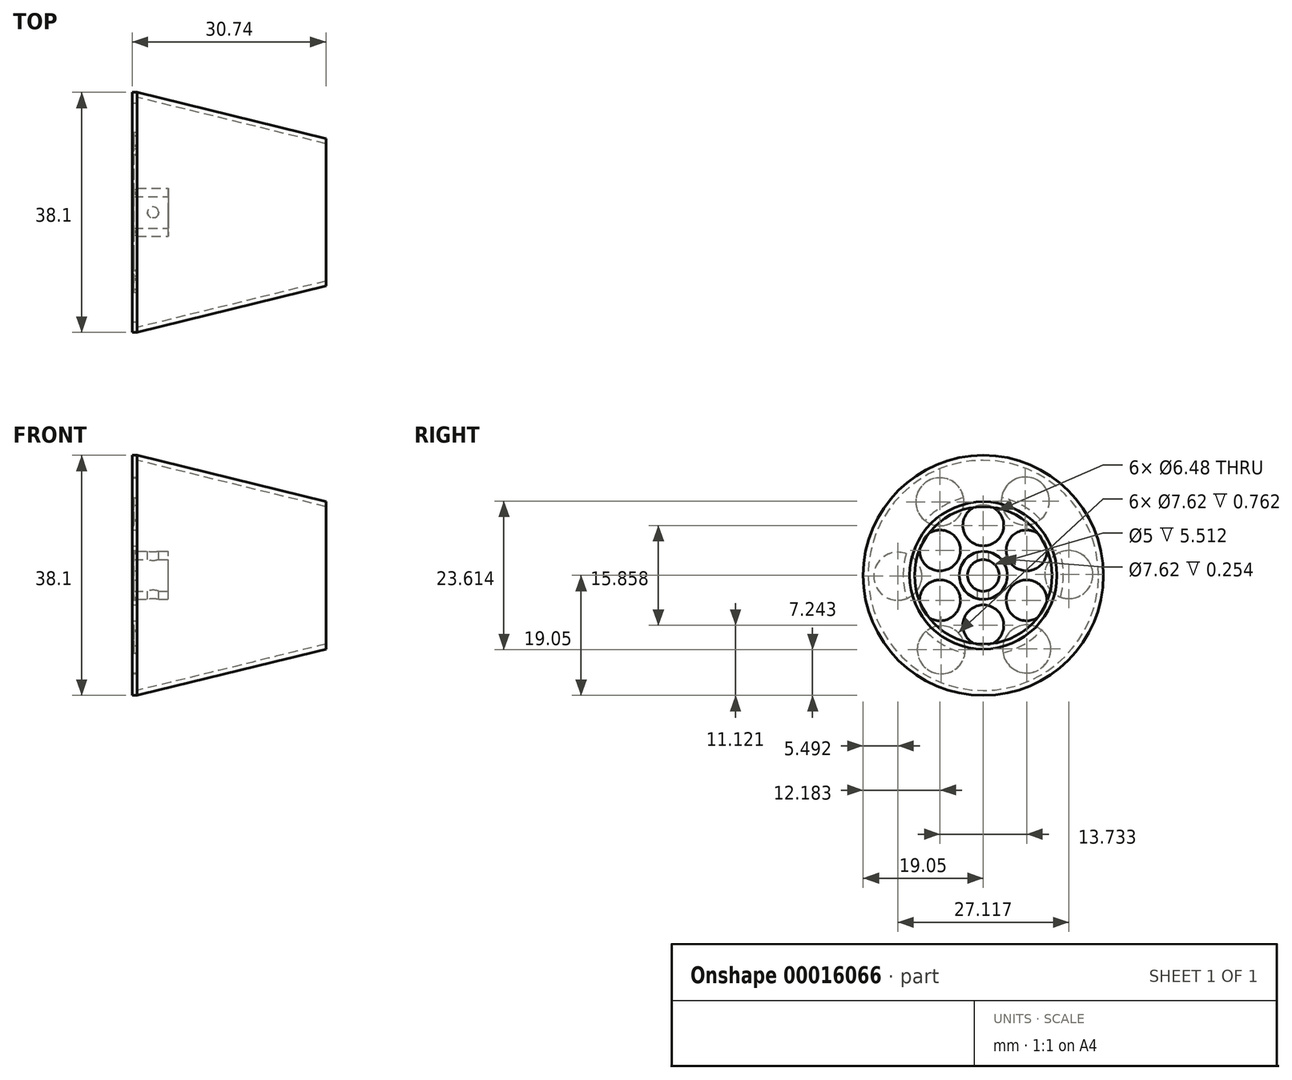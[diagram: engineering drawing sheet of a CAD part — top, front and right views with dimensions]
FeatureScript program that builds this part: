
annotation { "Feature Type Name" : "Feature", "Feature Type Description" : "" }
export const myFeature = defineFeature(function(context is Context, id is Id, definition is map)
    precondition{}
    {
        {
            var Q0;
            Q0=qCreatedBy(makeId("Right.planeOp"),FACE);
            var sketch = newSketch(context, id + "F0", { "sketchPlane" : qUnion([Q0])});
            skCircle(sketch, "E0", {"center": v(0, 0) * mm, "radius": 2.5 * mm});
            skCircle(sketch, "E1", {"center": v(0, 0) * mm, "radius": 3.81 * mm});
            skSolve(sketch);
        }
        {
            var Q0;
            Q0=makeQuery(id+"F0.imprint","IMPRINT",FACE,{"disambiguationData":[TD([[makeQuery(id+"F0.imprint","IMPRINT",EDGE,{"derivedFrom":sQuery(id+"F0.wireOp",EDGE,"E0")}),-1.0]])]});
            extrude(context, id + "F1", {"entities" : qUnion([Q0]), "oppositeDirection" : true, "depth" : 5 * mm});
        }
        {
            var Q0;
            Q0=qCreatedBy(makeId("Top.planeOp"),FACE);
            var sketch = newSketch(context, id + "F2", { "sketchPlane" : qUnion([Q0])});
            skCircle(sketch, "E2", {"center": v(-2.45, 0) * mm, "radius": 0.89 * mm});
            skSolve(sketch);
        }
        {
            var Q0;
            Q0=makeQuery(id+"F2.imprint","IMPRINT",FACE,{"disambiguationData":[TD([[makeQuery(id+"F2.imprint","IMPRINT",EDGE,{"derivedFrom":sQuery(id+"F2.wireOp",EDGE,"E2")}),1.0]])]});
            extrude(context, id + "F3", {"entities" : qUnion([Q0]), "operationType" : NewBodyOperationType.REMOVE, "endBound" : BoundingType.SYMMETRIC, "oppositeDirection" : true, "depth" : 25.4 * mm});
        }
        {
            var Q0;
            Q0=makeQuery(id+"F1.opExtrude","CAP_FACE",FACE,{"disambiguationData":[OSD([sQuery(id+"F0.wireOp",EDGE,"E0"),sQuery(id+"F0.wireOp",EDGE,"E1")])],"isStart":false});
            var sketch = newSketch(context, id + "F4", { "sketchPlane" : qUnion([Q0])});
            skCircle(sketch, "E3", {"center": v(0, 0) * mm, "radius": 12.7 * mm});
            skCircle(sketch, "E4", {"center": v(0, 7.93) * mm, "radius": 3.24 * mm});
            skCircle(sketch, "E5.1.0", {"center": v(-6.87, 3.96) * mm, "radius": 3.24 * mm});
            skCircle(sketch, "E5.2.0", {"center": v(-6.87, -3.96) * mm, "radius": 3.24 * mm});
            skCircle(sketch, "E5.3.0", {"center": v(0, -7.93) * mm, "radius": 3.24 * mm});
            skCircle(sketch, "E5.4.0", {"center": v(6.87, -3.96) * mm, "radius": 3.24 * mm});
            skCircle(sketch, "E5.5.0", {"center": v(6.87, 3.96) * mm, "radius": 3.24 * mm});
            skSolve(sketch);
        }
        {
            var Q0;
            Q0=makeQuery(id+"F4.imprint","IMPRINT",FACE,{"disambiguationData":[TD([[makeQuery(id+"F4.imprint","IMPRINT",EDGE,{"derivedFrom":makeQuery(id+"F1.opExtrude","CAP_EDGE",EDGE,{"disambiguationData":[OSD([sQuery(id+"F0.wireOp",EDGE,"E0")])],"isStart":false})}),1.0]])]});
            var Q1;
            Q1=makeQuery(id+"F4.imprint","IMPRINT",FACE,{"disambiguationData":[TD([[makeQuery(id+"F4.imprint","IMPRINT",EDGE,{"derivedFrom":sQuery(id+"F4.wireOp",EDGE,"E3")}),1.0]])]});
            extrude(context, id + "F5", {"entities" : qUnion([Q0, Q1]), "operationType" : NewBodyOperationType.ADD, "depth" : 0.5 * mm});
        }
        {
            var Q0;
            Q0=makeQuery(id+"F5.opExtrude","CAP_FACE",FACE,{"disambiguationData":[OSD([sQuery(id+"F0.wireOp",EDGE,"E0"),sQuery(id+"F4.wireOp",EDGE,"E3"),sQuery(id+"F4.wireOp",EDGE,"E4"),sQuery(id+"F4.wireOp",EDGE,"E5.1.0"),sQuery(id+"F4.wireOp",EDGE,"E5.2.0"),sQuery(id+"F4.wireOp",EDGE,"E5.3.0"),sQuery(id+"F4.wireOp",EDGE,"E5.4.0"),sQuery(id+"F4.wireOp",EDGE,"E5.5.0")])],"isStart":true});
            var sketch = newSketch(context, id + "F6", { "sketchPlane" : qUnion([Q0])});
            skCircle(sketch, "E6", {"center": v(0, 0) * mm, "radius": 12.7 * mm});
            skSolve(sketch);
        }
        {
            var Q0;
            Q0 = qSketchRegion(id + "F6", true);
            extrude(context, id + "F7", {"entities" : qUnion([Q0]), "depth" : 30 * mm, "hasDraft" : true, "draftAngle" : 2.5 * degree, "draftPullDirection" : true});
        }
        {
            var Q0;
            Q0=makeQuery(id+"F7.opExtrude","CAP_FACE",FACE,{"disambiguationData":[OSD([sQuery(id+"F6.wireOp",EDGE,"E6")])],"isStart":false});
            var Q1;
            Q1=makeQuery(id+"F7.opExtrude","CAP_FACE",FACE,{"disambiguationData":[OSD([sQuery(id+"F6.wireOp",EDGE,"E6")])],"isStart":true});
            var Q2;
            Q2=makeQuery(id+"F7.opExtrude","SWEPT_BODY",BODY,{"disambiguationData":[OSD([sQuery(id+"F6.wireOp",EDGE,"E6")])]});
            shell(context, id + "F8", {"entities" : qUnion([Q0, Q1]), "parts" : qUnion([Q2]), "thickness" : 0.76 * mm});
        }
        {
            var Q0;
            Q0=makeQuery(id+"F7.opExtrude","CAP_FACE",FACE,{"disambiguationData":[OSD([sQuery(id+"F6.wireOp",EDGE,"E6")])],"isStart":false});
            var sketch = newSketch(context, id + "F9", { "sketchPlane" : qUnion([Q0])});
            skCircle(sketch, "E7.0", {"center": v(0, 0) * mm, "radius": 11.4 * mm});
            skCircle(sketch, "E8", {"center": v(0, 0) * mm, "radius": 11.35 * mm});
            skSolve(sketch);
        }
        {
            var Q0;
            Q0=makeQuery(id+"F7.opExtrude","SWEPT_BODY",BODY,{"disambiguationData":[OSD([sQuery(id+"F6.wireOp",EDGE,"E6")])]});
            deleteBodies(context, id + "F10", {"entities" : qUnion([Q0])});
        }
        {
            var Q0;
            Q0=makeQuery(id+"F5.opExtrude","CAP_FACE",FACE,{"disambiguationData":[OSD([sQuery(id+"F0.wireOp",EDGE,"E0"),sQuery(id+"F4.wireOp",EDGE,"E3"),sQuery(id+"F4.wireOp",EDGE,"E4"),sQuery(id+"F4.wireOp",EDGE,"E5.1.0"),sQuery(id+"F4.wireOp",EDGE,"E5.2.0"),sQuery(id+"F4.wireOp",EDGE,"E5.3.0"),sQuery(id+"F4.wireOp",EDGE,"E5.4.0"),sQuery(id+"F4.wireOp",EDGE,"E5.5.0")])],"isStart":true});
            var sketch = newSketch(context, id + "F11", { "sketchPlane" : qUnion([Q0])});
            skCircle(sketch, "E9", {"center": v(0, 0) * mm, "radius": 19.05 * mm});
            skCircle(sketch, "E10", {"center": v(-6.9, 11.68) * mm, "radius": 3.81 * mm});
            skCircle(sketch, "E11.1.0", {"center": v(-13.56, -0.13) * mm, "radius": 3.81 * mm});
            skCircle(sketch, "E11.2.0", {"center": v(-6.67, -11.8) * mm, "radius": 3.81 * mm});
            skCircle(sketch, "E11.3.0", {"center": v(6.9, -11.68) * mm, "radius": 3.81 * mm});
            skCircle(sketch, "E11.4.0", {"center": v(13.56, 0.13) * mm, "radius": 3.81 * mm});
            skCircle(sketch, "E11.5.0", {"center": v(6.67, 11.8) * mm, "radius": 3.81 * mm});
            skSolve(sketch);
        }
        {
            var Q0;
            Q0=makeQuery(id+"F11.imprint","IMPRINT",FACE,{"disambiguationData":[TD([[makeQuery(id+"F11.imprint","IMPRINT",EDGE,{"derivedFrom":sQuery(id+"F11.wireOp",EDGE,"E9")}),1.0]])]});
            var Q1;
            Q1=makeQuery(id+"F11.imprint","IMPRINT",FACE,{"disambiguationData":[TD([[makeQuery(id+"F11.imprint","IMPRINT",EDGE,{"derivedFrom":makeQuery(id+"F5.opExtrude","CAP_EDGE",EDGE,{"disambiguationData":[OSD([sQuery(id+"F4.wireOp",EDGE,"E4")])],"isStart":true})}),1.0]])]});
            extrude(context, id + "F12", {"entities" : qUnion([Q0, Q1]), "operationType" : NewBodyOperationType.ADD, "oppositeDirection" : true, "depth" : 0.76 * mm});
        }
        {
            var Q0;
            {var subQ0=sQuery(id+"F4.wireOp",EDGE,"E4");var subQ1=sQuery(id+"F4.wireOp",EDGE,"E5.1.0");var subQ2=sQuery(id+"F4.wireOp",EDGE,"E5.2.0");var subQ3=sQuery(id+"F4.wireOp",EDGE,"E5.3.0");var subQ4=sQuery(id+"F4.wireOp",EDGE,"E5.4.0");var subQ5=sQuery(id+"F4.wireOp",EDGE,"E5.5.0");Q0=makeQuery(id+"F12.boolean.opBoolean","MERGE",FACE,{"derivedFrom":[makeQuery(id+"F5.opExtrude","CAP_FACE",FACE,{"disambiguationData":[OSD([sQuery(id+"F0.wireOp",EDGE,"E0"),sQuery(id+"F4.wireOp",EDGE,"E3"),subQ0,subQ1,subQ2,subQ3,subQ4,subQ5])],"isStart":true}),makeQuery(id+"F12.opExtrude","CAP_FACE",FACE,{"disambiguationData":[OSD([sQuery(id+"F0.wireOp",EDGE,"E1"),subQ0,subQ1,subQ2,subQ3,subQ4,subQ5,sQuery(id+"F11.wireOp",EDGE,"E9"),sQuery(id+"F11.wireOp",EDGE,"E10"),sQuery(id+"F11.wireOp",EDGE,"E11.1.0"),sQuery(id+"F11.wireOp",EDGE,"E11.2.0"),sQuery(id+"F11.wireOp",EDGE,"E11.3.0"),sQuery(id+"F11.wireOp",EDGE,"E11.4.0"),sQuery(id+"F11.wireOp",EDGE,"E11.5.0")])],"isStart":true})]});}
            var sketch = newSketch(context, id + "F13", { "sketchPlane" : qUnion([Q0])});
            skCircle(sketch, "E12", {"center": v(0, 0) * mm, "radius": 19.05 * mm});
            skSolve(sketch);
        }
        {
            var Q0;
            Q0 = qSketchRegion(id + "F13", true);
            extrude(context, id + "F14", {"entities" : qUnion([Q0]), "depth" : 29.97 * mm, "hasDraft" : true, "draftAngle" : 13.8 * degree, "draftPullDirection" : true});
        }
        {
            var Q0;
            Q0=makeQuery(id+"F14.opExtrude","CAP_FACE",FACE,{"disambiguationData":[OSD([sQuery(id+"F13.wireOp",EDGE,"E12")])],"isStart":false});
            var Q1;
            Q1=makeQuery(id+"F14.opExtrude","CAP_FACE",FACE,{"disambiguationData":[OSD([sQuery(id+"F13.wireOp",EDGE,"E12")])],"isStart":true});
            var Q2;
            Q2=makeQuery(id+"F14.opExtrude","SWEPT_BODY",BODY,{"disambiguationData":[OSD([sQuery(id+"F13.wireOp",EDGE,"E12")])]});
            shell(context, id + "F15", {"entities" : qUnion([Q0, Q1]), "parts" : qUnion([Q2]), "thickness" : 0.76 * mm});
        }
    });
